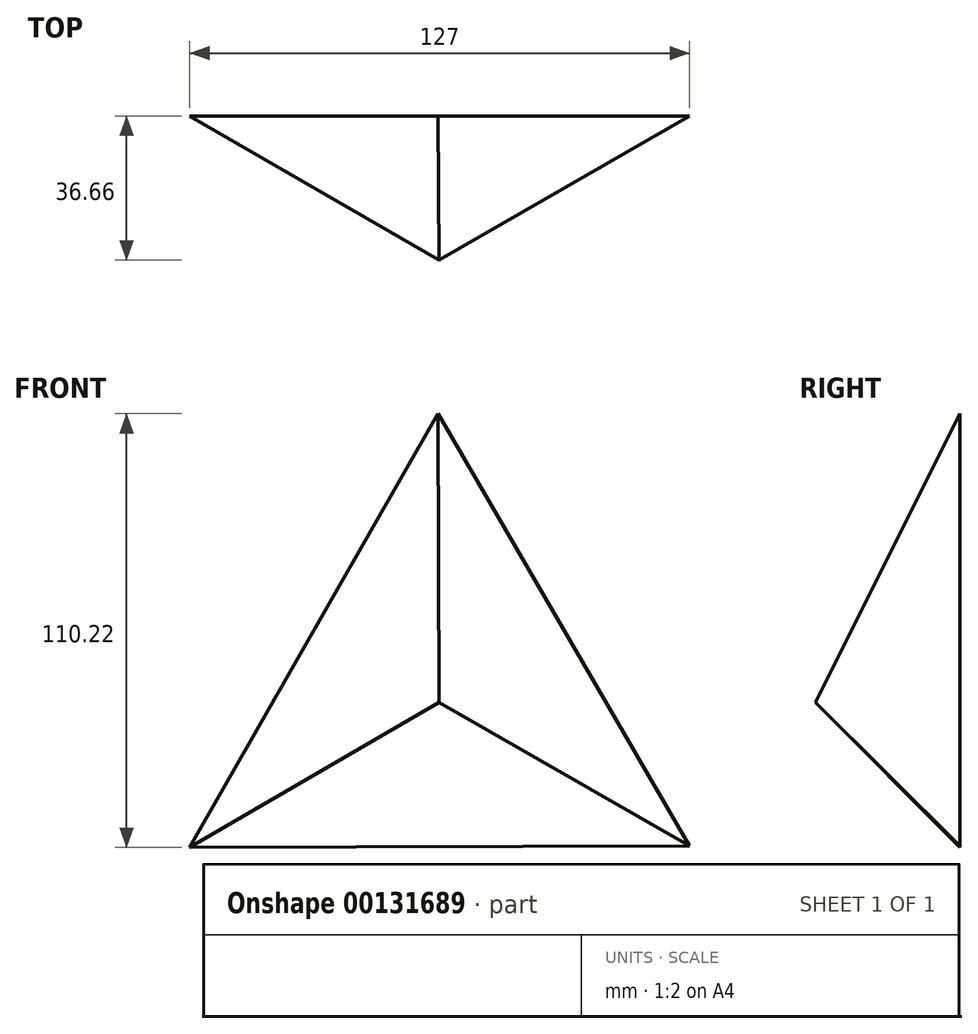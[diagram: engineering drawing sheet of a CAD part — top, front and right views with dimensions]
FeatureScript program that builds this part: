
annotation { "Feature Type Name" : "Feature", "Feature Type Description" : "" }
export const myFeature = defineFeature(function(context is Context, id is Id, definition is map)
    precondition{}
    {
        {
            var Q0;
            Q0=qCreatedBy(makeId("Front.planeOp"),FACE);
            var sketch = newSketch(context, id + "F0", { "sketchPlane" : qUnion([Q0])});
            skCircle(sketch, "E0.cCircle", {"center": v(0, 0) * mm, "radius": 36.66 * mm, "construction": true});
            skLineSegment(sketch, "E0.0", {"start": v(-63.36, -36.9) * mm, "end": v(-0.28, 73.32) * mm});
            skLineSegment(sketch, "E0.1", {"start": v(-0.28, 73.32) * mm, "end": v(63.64, -36.42) * mm});
            skLineSegment(sketch, "E0.2", {"start": v(63.64, -36.42) * mm, "end": v(-63.36, -36.9) * mm});
            skPoint(sketch, "E0.0.midPoint", {"position": v(-31.82, 18.2) * mm});
            skSolve(sketch);
        }
        {
            var Q0;
            Q0 = qSketchRegion(id + "F0", true);
            extrude(context, id + "F1", {"entities" : qUnion([Q0]), "depth" : 254 * mm, "hasDraft" : true, "draftAngle" : 45 * degree, "draftPullDirection" : true});
        }
    });
